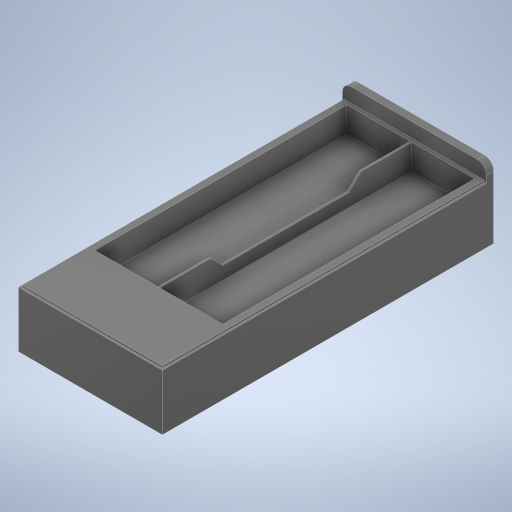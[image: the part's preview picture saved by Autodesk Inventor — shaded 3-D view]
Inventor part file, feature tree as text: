
AUTODESK INVENTOR PART (.ipt)
format: ipt  version: 2024 (Build 280153000, 153)  size: 300,032 bytes
history: native  units: in
note: dims shown in document units (in); Inventor stores cm internally (conversion verified against a paired STEP export)
features: extrude x5, sketch x5, fillet x1
ambient origin geometry x8: Origin, YZ Plane, XZ Plane, XY Plane, X Axis, Y Axis, Z Axis, Center Point
bodies: Solid1 (feature_tree)
feature tree (11):
  extrude  "Extrusion1"  Depth=3.622in
  extrude  "Extrusion2"  Depth=3.5433in
  extrude  "Extrusion3"  Depth=0.689in
  extrude  "Extrusion4"  Depth=0.0886in
  fillet  "Fillet1"  Radius=0.0394in
  extrude  "Extrusion5"  Depth=0.0886in
  sketch  "Sketch1"  dims[d0=1.5748in d1=3.622in]
  sketch  "Sketch2"  dims[d2=0.7874in d3=0.0in d4=3.5433in]
  sketch  "Sketch3"  dims[d5=0.1575in d6=0.0in d7=0.689in]
  sketch  "Sketch4"  dims[d8=2.7559in d9=0.0886in d10=0.0394in]
  sketch  "Sketch5"  dims[d11=0.689in d12=0.0886in d13=0.0394in d14=0.2756in d15=0.0in d16=45.0deg d17=45.0deg d18=0.689in d19=0.689in d20=0.0in d21=0.0in d22=0.0984in d23=0.0197in d24=0.0197in d25=0.0197in d27=0.0197in d28=0.0in]
